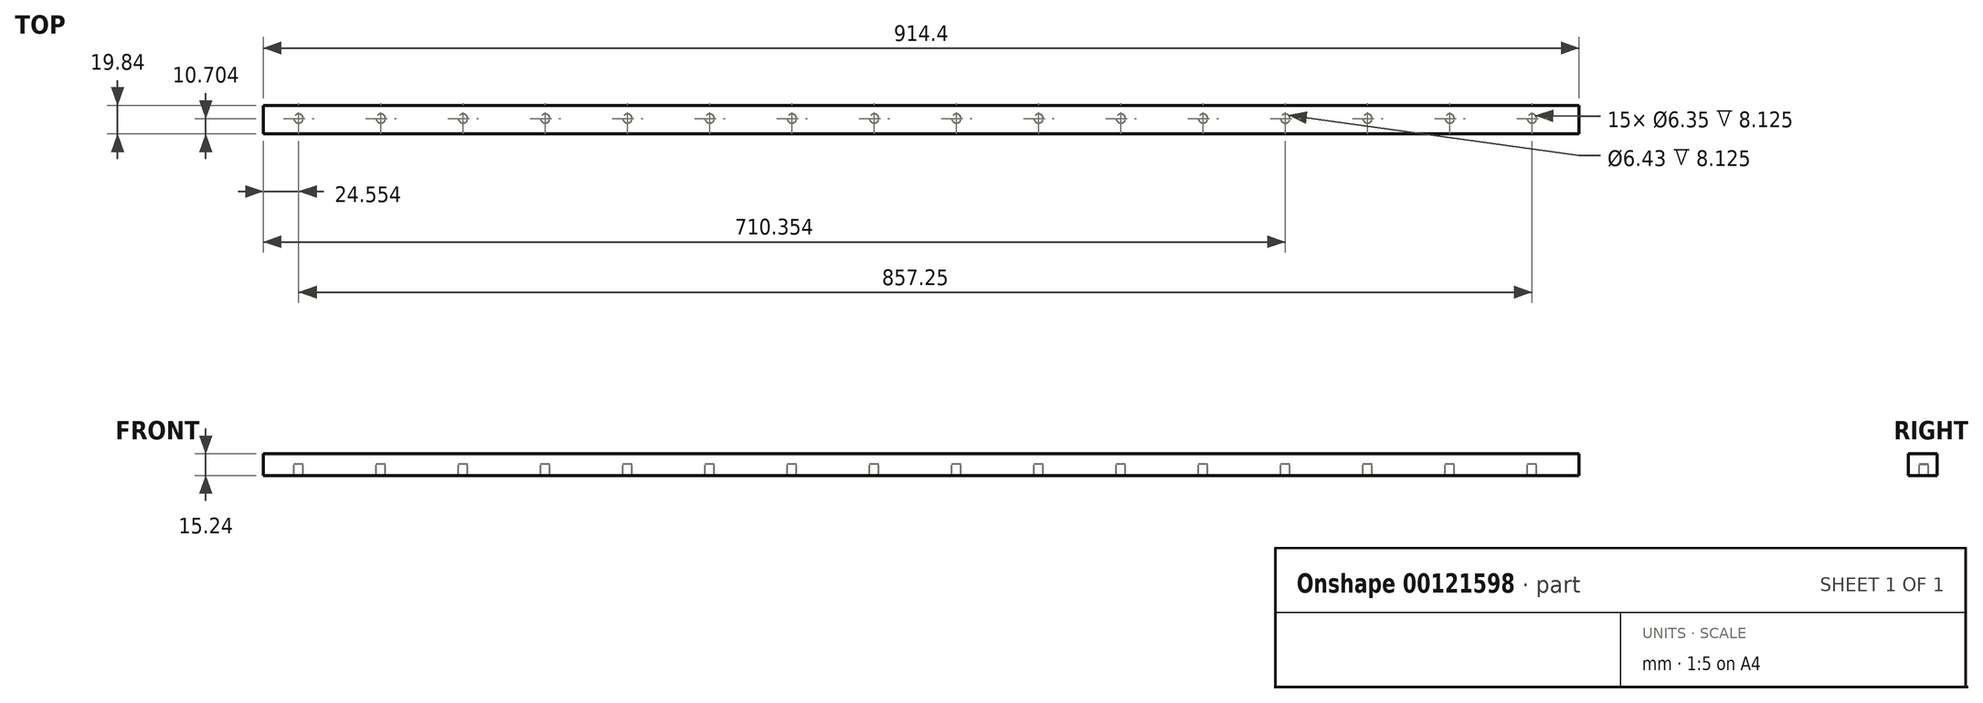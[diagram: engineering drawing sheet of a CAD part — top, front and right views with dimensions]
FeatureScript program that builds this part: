
annotation { "Feature Type Name" : "Feature", "Feature Type Description" : "" }
export const myFeature = defineFeature(function(context is Context, id is Id, definition is map)
    precondition{}
    {
        {
            var Q0;
            Q0=qCreatedBy(makeId("Front.planeOp"),FACE);
            var sketch = newSketch(context, id + "F0", { "sketchPlane" : qUnion([Q0])});
            skLineSegment(sketch, "E0", {"start": v(-125.1, 7.12) * mm, "end": v(789.3, 7.12) * mm});
            skLineSegment(sketch, "E1", {"start": v(789.3, 7.12) * mm, "end": v(789.3, -8.12) * mm});
            skLineSegment(sketch, "E2", {"start": v(789.3, -8.12) * mm, "end": v(-125.1, -8.12) * mm});
            skLineSegment(sketch, "E3", {"start": v(-125.1, -8.12) * mm, "end": v(-125.1, 7.12) * mm});
            skSolve(sketch);
        }
        {
            var Q0;
            Q0 = qSketchRegion(id + "F0", true);
            extrude(context, id + "F1", {"entities" : qUnion([Q0]), "depth" : 19.84 * mm});
        }
        {
            var Q0;
            Q0=qCreatedBy(makeId("Top.planeOp"),FACE);
            var sketch = newSketch(context, id + "F2", { "sketchPlane" : qUnion([Q0])});
            skCircle(sketch, "E4", {"center": v(756.7, -9.14) * mm, "radius": 3.18 * mm});
            skCircle(sketch, "E5", {"center": v(699.55, -9.14) * mm, "radius": 3.18 * mm});
            skCircle(sketch, "E6", {"center": v(642.4, -9.14) * mm, "radius": 3.18 * mm});
            skCircle(sketch, "E7", {"center": v(585.25, -9.14) * mm, "radius": 3.21 * mm});
            skCircle(sketch, "E8", {"center": v(528.1, -9.14) * mm, "radius": 3.18 * mm});
            skCircle(sketch, "E9", {"center": v(470.95, -9.14) * mm, "radius": 3.18 * mm});
            skCircle(sketch, "E10", {"center": v(413.8, -9.14) * mm, "radius": 3.18 * mm});
            skCircle(sketch, "E11", {"center": v(356.65, -9.14) * mm, "radius": 3.18 * mm});
            skCircle(sketch, "E12", {"center": v(299.5, -9.14) * mm, "radius": 3.18 * mm});
            skCircle(sketch, "E13", {"center": v(242.35, -9.14) * mm, "radius": 3.18 * mm});
            skCircle(sketch, "E14", {"center": v(185.2, -9.14) * mm, "radius": 3.18 * mm});
            skCircle(sketch, "E15", {"center": v(128.05, -9.14) * mm, "radius": 3.18 * mm});
            skCircle(sketch, "E16", {"center": v(70.9, -9.14) * mm, "radius": 3.18 * mm});
            skCircle(sketch, "E17", {"center": v(13.75, -9.14) * mm, "radius": 3.18 * mm});
            skCircle(sketch, "E18", {"center": v(-43.4, -9.14) * mm, "radius": 3.18 * mm});
            skCircle(sketch, "E19", {"center": v(-100.55, -9.14) * mm, "radius": 3.18 * mm});
            skSolve(sketch);
        }
        {
            var Q0;
            Q0 = qSketchRegion(id + "F2", true);
            extrude(context, id + "F3", {"entities" : qUnion([Q0]), "operationType" : NewBodyOperationType.REMOVE, "endBound" : BoundingType.THROUGH_ALL, "oppositeDirection" : true, "depth" : 25.4 * mm});
        }
    });
